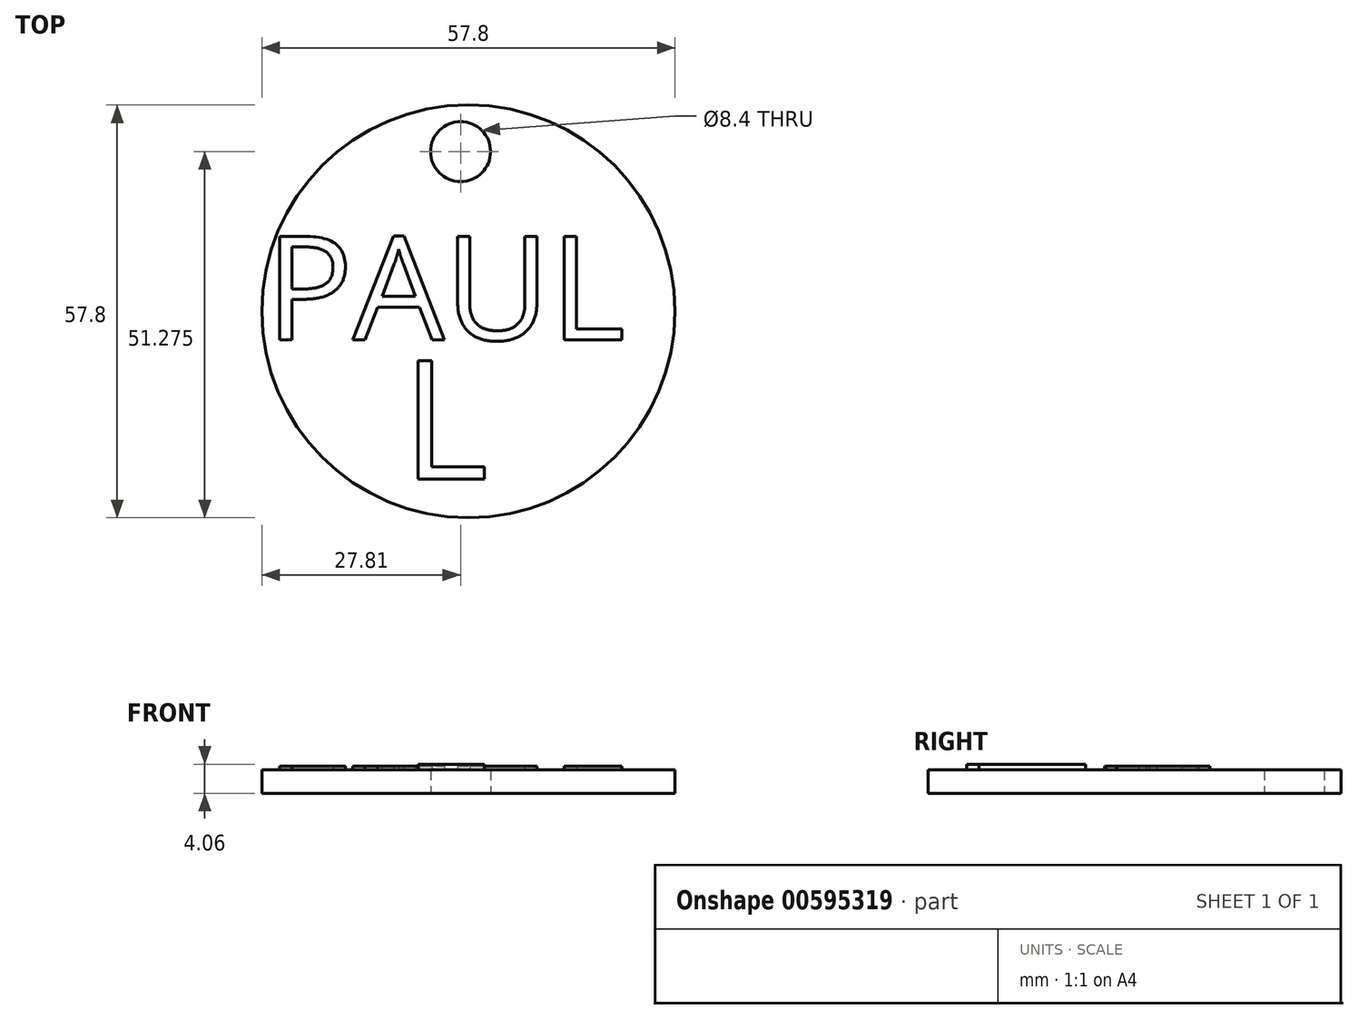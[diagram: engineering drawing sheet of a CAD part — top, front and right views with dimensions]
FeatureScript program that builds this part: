
annotation { "Feature Type Name" : "Feature", "Feature Type Description" : "" }
export const myFeature = defineFeature(function(context is Context, id is Id, definition is map)
    precondition{}
    {
        {
            var Q0;
            Q0=qCreatedBy(makeId("Top.planeOp"),FACE);
            var sketch = newSketch(context, id + "F0", { "sketchPlane" : qUnion([Q0])});
            skCircle(sketch, "E0", {"center": v(0, 0) * mm, "radius": 28.9 * mm});
            skSolve(sketch);
        }
        {
            var Q0;
            Q0 = qSketchRegion(id + "F0", true);
            extrude(context, id + "F1", {"entities" : qUnion([Q0]), "depth" : 3.3 * mm, "offsetDistance" : 25.4 * mm});
        }
        {
            var Q0;
            Q0=qCreatedBy(makeId("Top.planeOp"),FACE);
            var sketch = newSketch(context, id + "F2", { "sketchPlane" : qUnion([Q0])});
            skText(sketch, "E1", { "text": "PAUL", "fontName": "OpenSans-Regular.ttf"});
            const initialGuessF2  = {"E1": [-0.02837, -0.004, 1, 0, 0.0146]};
            skSetInitialGuess(sketch, initialGuessF2);
            skSolve(sketch);
        }
        {
            var Q0;
            Q0 = qSketchRegion(id + "F2", true);
            extrude(context, id + "F3", {"entities" : qUnion([Q0]), "operationType" : NewBodyOperationType.ADD, "depth" : 3.8 * mm, "offsetDistance" : 25.4 * mm});
        }
        {
            var Q0;
            Q0=qCreatedBy(makeId("Top.planeOp"),FACE);
            var sketch = newSketch(context, id + "F4", { "sketchPlane" : qUnion([Q0])});
            skCircle(sketch, "E2", {"center": v(-1.1, 22.38) * mm, "radius": 4.2 * mm});
            skSolve(sketch);
        }
        {
            var Q0;
            Q0 = qSketchRegion(id + "F4", true);
            extrude(context, id + "F5", {"entities" : qUnion([Q0]), "operationType" : NewBodyOperationType.REMOVE, "depth" : 8.38 * mm, "offsetDistance" : 25.4 * mm});
        }
        {
            var Q0;
            {var subQ0=sQuery(id+"F0.wireOp",EDGE,"E0");Q0=makeQuery(id+"F3.boolean.opBoolean","SPLIT",FACE,{"disambiguationData":[TD([makeQuery(id+"F1.opExtrude","SWEPT_FACE",FACE,{"disambiguationData":[OSD([subQ0])]})])],"derivedFrom":makeQuery(id+"F1.opExtrude","CAP_FACE",FACE,{"disambiguationData":[OSD([subQ0])],"isStart":false})});}
            var sketch = newSketch(context, id + "F6", { "sketchPlane" : qUnion([Q0])});
            skText(sketch, "E3", { "text": "L", "fontName": "OpenSans-Regular.ttf"});
            const initialGuessF6  = {"E3": [-0.00935, -0.0235, 1, 0, 0.01677]};
            skSetInitialGuess(sketch, initialGuessF6);
            skSolve(sketch);
        }
        {
            var Q0;
            Q0 = qSketchRegion(id + "F6", true);
            extrude(context, id + "F7", {"entities" : qUnion([Q0]), "operationType" : NewBodyOperationType.ADD, "depth" : 0.76 * mm, "offsetDistance" : 25.4 * mm});
        }
    });
